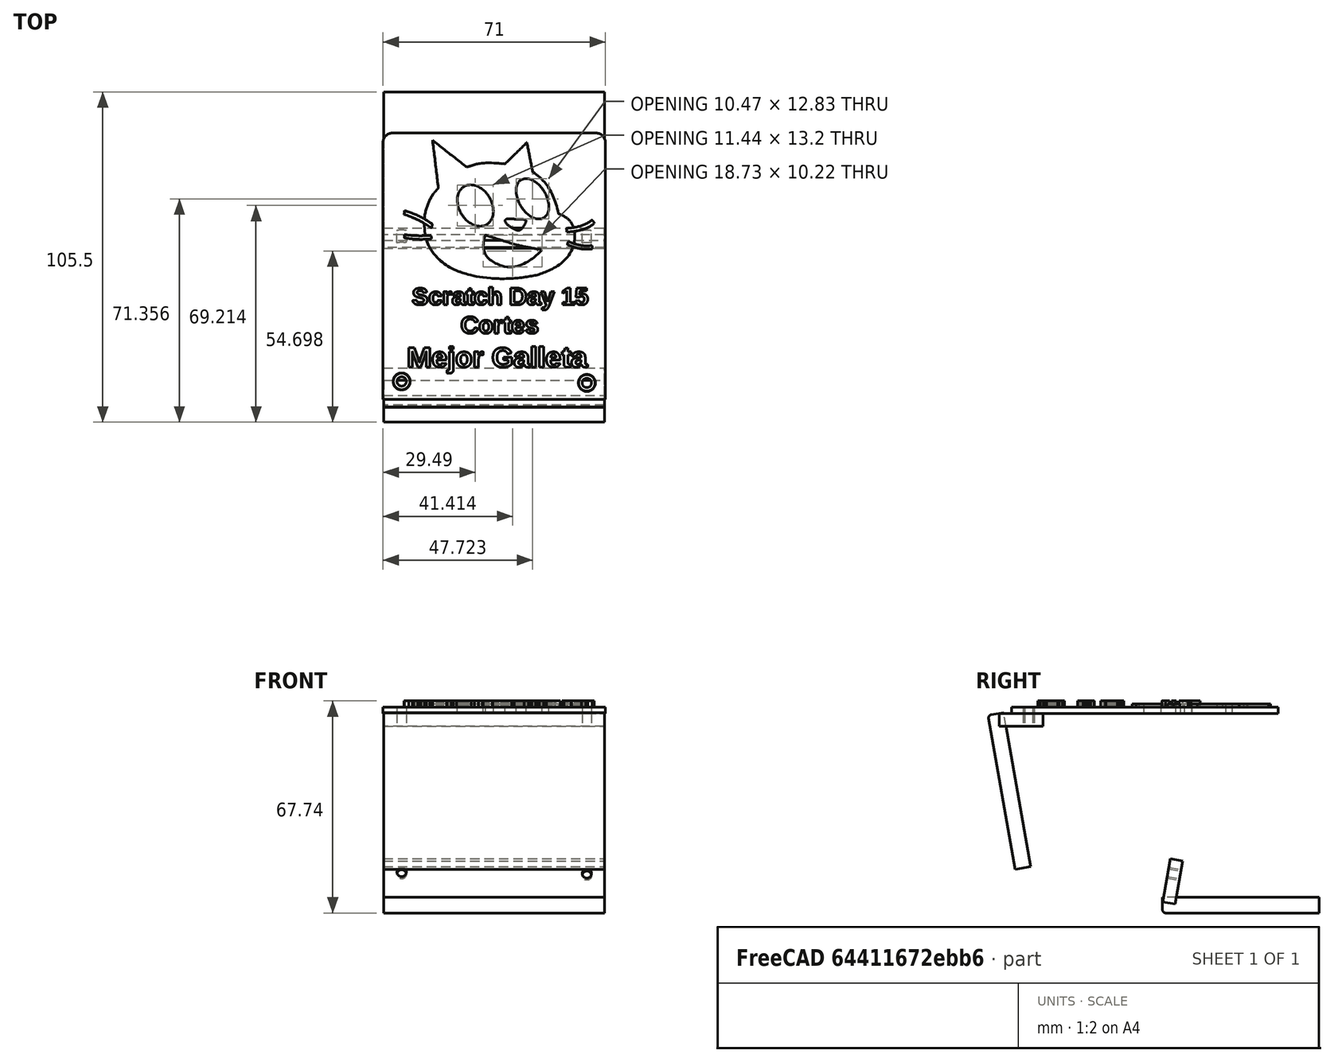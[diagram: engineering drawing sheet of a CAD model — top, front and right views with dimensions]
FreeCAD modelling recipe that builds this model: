
FCSTD DOCUMENT  (FreeCAD 0.14R3702 (Git))
Label: Trofeo Scratch2
License: CC-BY 3.0
LicenseURL: http://creativecommons.org/licenses/by/3.0/
objects: Part::Feature×13, Part::Extrusion×12, Part::MultiFuse×4, Part::Cut×4, Part::Box×3, Part::Part2DObjectPython×3, Part::Fillet×2
note: 41 computed .brp shape members not serialized (recipe doc carries the construction recipe); baked Part::Feature solids carry a one-line shape summary decoded from their .brp

FEATURE [Part::Feature] path
  shape: bbox 48.25 x 45.35 x 2e-07 mm, 0 faces, 0 solids (baked)
FEATURE [Part::Feature] path3973_
  shape: bbox 12.16 x 13.86 x 2e-07 mm, 0 faces, 0 solids (baked)
FEATURE [Part::Feature] path3981_
  shape: bbox 11.18 x 13.57 x 2e-07 mm, 0 faces, 0 solids (baked)
FEATURE [Part::Feature] path4045_
  shape: bbox 19.5 x 11.04 x 2e-07 mm, 0 faces, 0 solids (baked)
FEATURE [Part::Feature] path3993_1_
  shape: bbox 6.742 x 3.801 x 2e-07 mm, 1 faces, 0 solids (baked)
FEATURE [Part::Feature] path001
  shape: bbox 9.018 x 5.518 x 2e-07 mm, 0 faces, 0 solids (baked)
FEATURE [Part::Feature] path002
  shape: bbox 8.682 x 1.641 x 2e-07 mm, 0 faces, 0 solids (baked)
FEATURE [Part::Feature] path003
  shape: bbox 8.914 x 3.82 x 2e-07 mm, 0 faces, 0 solids (baked)
FEATURE [Part::Feature] path004
  shape: bbox 7.988 x 2.613 x 2e-07 mm, 0 faces, 0 solids (baked)
FEATURE [Part::Box] Box  label="Cubo"
  Height = 2
  Length = 71
  Placement = pos=(-37.7424,-57.9426,-0.991511) rot=(0,0,1;0rad)
  Width = 85
FEATURE [Part::Part2DObjectPython] ShapeString002  # Draft 2D object (typed FeaturePython)
  FontFile = <path>
  Placement = pos=(-13.454,-24.3602,0) rot=(0,0,1;0rad)
  Size = 6
  String = Scratch Day 15
  Tracking = 0
FEATURE [Part::Extrusion] Extrude024
  Base = -> ShapeString002
  Dir = (0,0,2)
  Placement = pos=(-15.006,-3.48125,0.999991) rot=(0,0,1;0rad)
  Solid = true
FEATURE [Part::Part2DObjectPython] ShapeString004  # Draft 2D object (typed FeaturePython)
  FontFile = <path>
  Placement = pos=(-16.454,-24.3602,0) rot=(0,0,1;0rad)
  Size = 7
  String = Mejor Galleta
  Tracking = 0
FEATURE [Part::Extrusion] Extrude026  label="TextoEstruido"
  Base = -> ShapeString004
  Dir = (0,0,2)
  Placement = pos=(-13.6044,-23.3916,0.999858) rot=(0,0,1;0rad)
  Solid = true
FEATURE [Part::Extrusion] Extrude028
  Base = -> path004
  Dir = (0,0,3)
  Solid = true
FEATURE [Part::Extrusion] Extrude029
  Base = -> path001
  Dir = (0,0,3)
  Solid = true
FEATURE [Part::Extrusion] Extrude030
  Base = -> path002
  Dir = (0,0,3)
  Solid = true
FEATURE [Part::Extrusion] Extrude032
  Base = -> path3973_
  Dir = (0,0,6)
  Solid = true
FEATURE [Part::Extrusion] Extrude033
  Base = -> path003
  Dir = (0,0,3)
  Solid = true
FEATURE [Part::Extrusion] Extrude034
  Base = -> path3993_1_
  Dir = (0,0,6)
  Solid = true
FEATURE [Part::Extrusion] Extrude035
  Base = -> path4045_
  Dir = (0,0,6)
  Solid = true
FEATURE [Part::Extrusion] Extrude036
  Base = -> path3981_
  Dir = (0,0,6)
  Solid = true
FEATURE [Part::Extrusion] Extrude037
  Base = -> path
  Dir = (0,0,2)
  Solid = true
FEATURE [Part::Part2DObjectPython] ShapeString005  # Draft 2D object (typed FeaturePython)
  FontFile = <path>
  Placement = pos=(-13.454,-24.3602,0) rot=(0,0,1;0rad)
  Size = 6
  String = Cortes
  Tracking = 0
FEATURE [Part::Extrusion] Extrude038
  Base = -> ShapeString005
  Dir = (0,0,2)
  Placement = pos=(0.501886,-12.5972,0.999962) rot=(0,0,1;0rad)
  Solid = true
FEATURE [Part::MultiFuse] Fusion004
  Placement = pos=(0,0,-1) rot=(0,0,1;0rad)
  Shapes = -> [Extrude034,Extrude035,Extrude032,Extrude036]
FEATURE [Part::Fillet] Fillet
  Base = -> Box
  Edges = 2 edges r=3: [Edge3,Edge7]
FEATURE [Part::MultiFuse] Fusion005
  Shapes = -> [Fillet,Extrude033,Extrude028,Extrude029,Extrude030,Extrude037,Extrude038,Extrude026,Extrude024]
FEATURE [Part::Cut] Cut  label="Frontal"
  Base = -> Fusion005
  Tool = -> Fusion004
FEATURE [Part::Feature] Part__Feature  label="Chamfer005"
  Placement = pos=(27.2337,-52.621,20.2591) rot=(0,0,1;0rad)
  shape: bbox 6.35 x 6.35 x 2.4 mm, 29 faces (baked)
FEATURE [Part::Feature] Part__Feature001  label="Chamfer002"
  Placement = pos=(-31.7737,-52.284,20.2591) rot=(0,0,1;0rad)
  shape: bbox 6.35 x 6.35 x 2.4 mm, 29 faces (baked)
FEATURE [Part::Feature] Part__Feature002  label="Chamfer004"
  Placement = pos=(27.3367,-52.7409,28.9364) rot=(0,0,1;0rad)
  shape: bbox 5.5 x 5.5 x 15 mm, 16 faces (baked)
FEATURE [Part::Feature] Part__Feature003  label="Chamfer003"
  Placement = pos=(-31.7766,-52.2852,28.9365) rot=(0,0,1;0rad)
  shape: bbox 5.5 x 5.5 x 15 mm, 16 faces (baked)
FEATURE [Part::MultiFuse] Fusion  label="tornilleria futaba"
  Placement = pos=(0,0,-28) rot=(0,0,1;0rad)
  Shapes = -> [Part__Feature003,Part__Feature002,Part__Feature001,Part__Feature]
FEATURE [Part::Box] Box001  label="Cubo001"
  Height = 4
  Length = 70.5
  Placement = pos=(-37.5258,-61.9669,-5.08684) rot=(0,0,1;0rad)
  Width = 14
FEATURE [Part::Box] Box002  label="Cubo002"
  Height = 50
  Length = 70.5
  Placement = pos=(-37.5646,-56.778,-50.8302) rot=(1,0,0;0.174533rad)
  Width = 5
FEATURE [Part::MultiFuse] Fusion006
  Shapes = -> [Box001,Box002]
FEATURE [Part::Fillet] Fillet001
  Base = -> Fusion006
  Edges = 1 edges r=1: [Edge28]
FEATURE [Part::Cut] Cut001
  Base = -> Cut
  Tool = -> Fusion
FEATURE [Part::Cut] Cut002
  Base = -> Fillet001
  Tool = -> Fusion
FEATURE [Part::Cut] Cut003
  Base = -> Fillet001
  Placement = pos=(0,0,0) rot=(1,0,0;1.39626rad)
  Tool = -> Fusion
note: 3 file-system paths scrubbed to <path> (originals preserved in the JSON sidecar)
